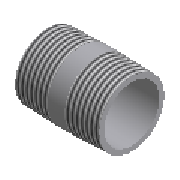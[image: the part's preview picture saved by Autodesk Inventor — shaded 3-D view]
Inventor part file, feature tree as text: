
AUTODESK INVENTOR PART (.ipt)
format: ipt  version: 2023.2 (Build 272271030, 271C)  size: 182,272 bytes
history: native  units: mm (DEFAULTED — no unit token found)
features: other x6, revolve x1, sketch x1
ambient origin geometry x8: Origin, YZ Plane, XZ Plane, XY Plane, X Axis, Y Axis, Z Axis, Center Point
bodies: Solid1 (feature_tree)
feature tree (8):
  revolve  "Revolution1"  [1 undecoded]
  other  "Work Point3"
  other  "Work Point4"
  other  "Work Axis1"
  other  "Work Point5"
  other  "Work Axis2"
  other  "Work Point6"
  sketch  "Sketch1"  dims[d12=90.0deg d1=0.312398mm d2=58.0mm d3=26.1mm d4=0.0mm d5=26.1mm d6=0.0mm d7=15.88mm d8=59.614mm d57=52.9mm d60=23.38mm d62=0.0mm]
note: 1 required parameter value undecoded (feature->parameter linkage not recoverable at this tier; creation-order binding heuristic only, values carry confidence <= 0.55)
